# Revit family: Kohler Panache 17640IN-S-00 Family
name_source: partatom
category: Plumbing Fixtures
revit_build: Autodesk Revit 2018 (Build: 20180329_1100(x64)
units: mm (PartAtom-declared; Revit-internal decimal feet)

## family parameters
Always vertical = Yes
Cut with Voids When Loaded = No
OmniClass Number = 23.45.00.00
OmniClass Title = Sanitary, Laundry, and Cleaning Equipment
Part Type = Normal
Room Calculation Point = No
Round Connector Dimension = Use Diameter
Shared = No
Work Plane-Based = No

## types (1)
- Kohler 17640IN-S-00
    Description = Two-Piece toilet with Quiet-Close seat cover in white
    Height = 775 mm  [stored 2.54265 ft]
    Length = 370 mm  [stored 1.21391 ft]
    Manufacturer = Kohler
    Material = Render Material 255-255-255
    Model = Kohler Panache 17640IN-S-00
    URL = http://www.us.kohler.com
    Width = 185 mm  [stored 0.606955 ft]

note: [stored X ft] marks values corroborated as IEEE doubles in the binary element streams (Revit-internal decimal feet)

## geometry (parser evidence)
native form markers: Sweep x3
no freeform markers — native parametric forms only
